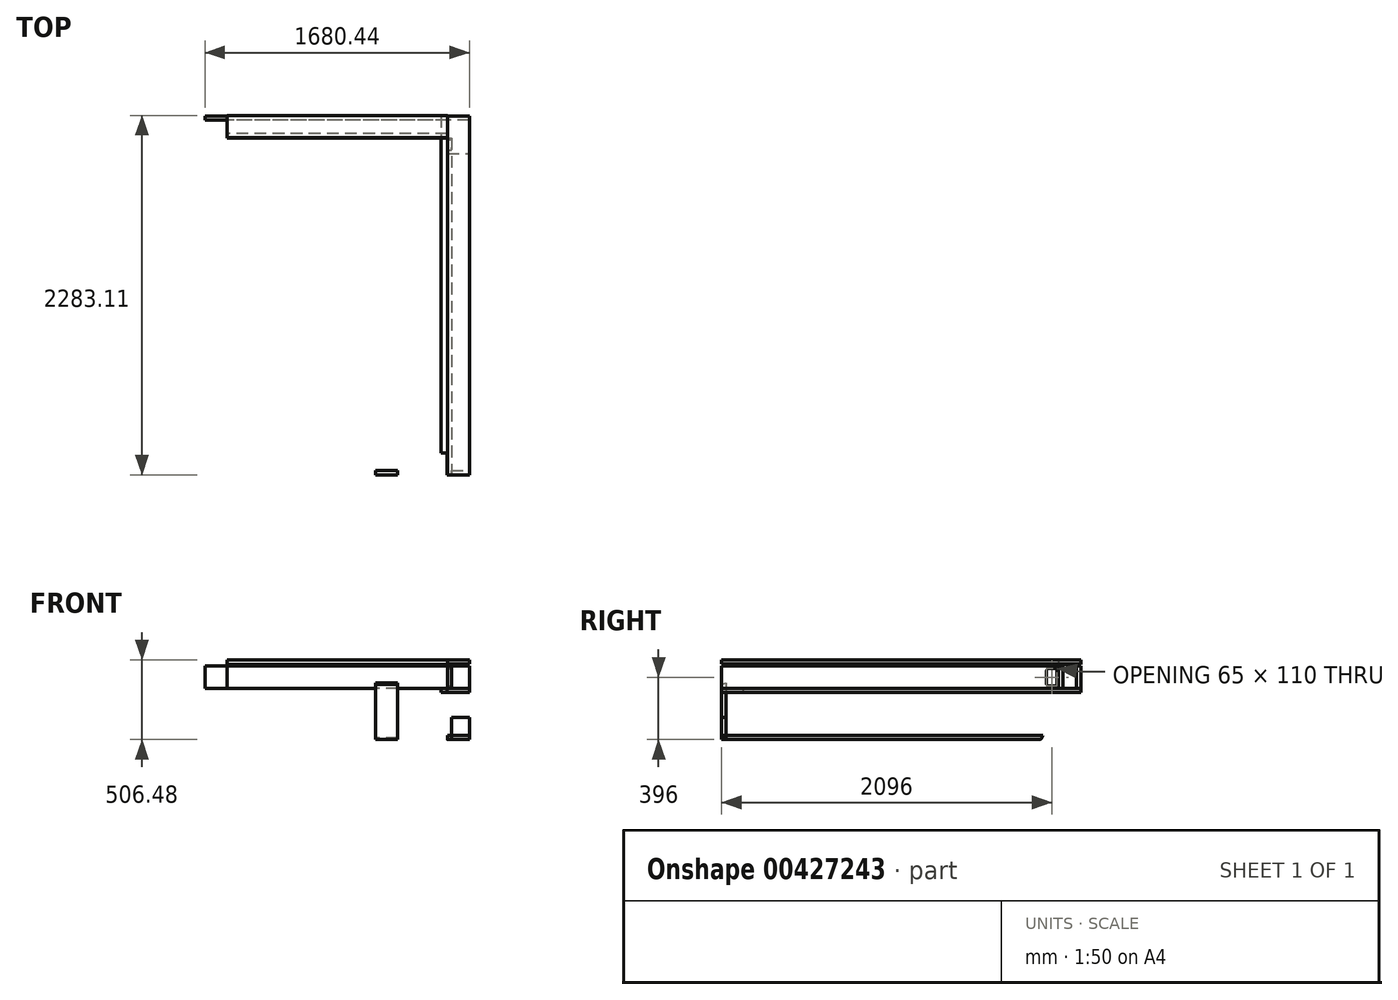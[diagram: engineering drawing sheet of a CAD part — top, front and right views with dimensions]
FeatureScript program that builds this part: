
annotation { "Feature Type Name" : "Feature", "Feature Type Description" : "" }
export const myFeature = defineFeature(function(context is Context, id is Id, definition is map)
    precondition{}
    {
        {
            var Q0;
            Q0=qCreatedBy(makeId("Front.planeOp"),FACE);
            var sketch = newSketch(context, id + "F0", { "sketchPlane" : qUnion([Q0])});
            skLineSegment(sketch, "E0.bottom", {"start": v(700, 0) * mm, "end": v(840, 0) * mm});
            skLineSegment(sketch, "E0.top", {"start": v(700, 26) * mm, "end": v(840, 26) * mm});
            skLineSegment(sketch, "E0.left", {"start": v(700, 0) * mm, "end": v(700, 26) * mm});
            skLineSegment(sketch, "E0.right", {"start": v(840, 0) * mm, "end": v(840, 26) * mm});
            skSolve(sketch);
        }
        {
            var Q0;
            Q0=makeQuery(id+"F0.imprint","IMPRINT",FACE,{"disambiguationData":[TD([[makeQuery(id+"F0.imprint","IMPRINT",EDGE,{"derivedFrom":sQuery(id+"F0.wireOp",EDGE,"E0.bottom")}),1.0]])]});
            extrude(context, id + "F1", {"entities" : qUnion([Q0]), "oppositeDirection" : true, "depth" : 2040 * mm});
        }
        {
            var Q0;
            Q0=makeQuery(id+"F1.opExtrude","CAP_EDGE",EDGE,{"disambiguationData":[OSD([sQuery(id+"F0.wireOp",EDGE,"E0.bottom")])],"isStart":true});
            var Q1;
            Q1=makeQuery(id+"F1.opExtrude","CAP_EDGE",EDGE,{"disambiguationData":[OSD([sQuery(id+"F0.wireOp",EDGE,"E0.bottom")])],"isStart":false});
            chamfer(context, id + "F2", {"entities" : qUnion([Q0, Q1]), "chamferType" : ChamferType.OFFSET_ANGLE, "width" : 26 * mm, "oppositeDirection" : false, "angle" : 20 * degree, "tangentPropagation" : true});
        }
        {
            var Q0;
            Q0=qCreatedBy(makeId("Front.planeOp"),FACE);
            var sketch = newSketch(context, id + "F3", { "sketchPlane" : qUnion([Q0])});
            skLineSegment(sketch, "E1.bottom", {"start": v(660, 300) * mm, "end": v(840, 300) * mm});
            skLineSegment(sketch, "E1.top", {"start": v(660, 326) * mm, "end": v(840, 326) * mm});
            skLineSegment(sketch, "E1.left", {"start": v(660, 300) * mm, "end": v(660, 326) * mm});
            skLineSegment(sketch, "E1.right", {"start": v(840, 300) * mm, "end": v(840, 326) * mm});
            skSolve(sketch);
        }
        {
            var Q0;
            Q0=makeQuery(id+"F3.imprint","IMPRINT",FACE,{"disambiguationData":[TD([[makeQuery(id+"F3.imprint","IMPRINT",EDGE,{"derivedFrom":sQuery(id+"F3.wireOp",EDGE,"E1.bottom")}),1.0]])]});
            extrude(context, id + "F4", {"entities" : qUnion([Q0]), "oppositeDirection" : true, "depth" : (2000 + (2 * 140)) * mm});
        }
        {
            var Q0;
            Q0=makeQuery(id+"F4.opExtrude","SWEPT_FACE",FACE,{"disambiguationData":[OSD([sQuery(id+"F3.wireOp",EDGE,"E1.top")])]});
            var sketch = newSketch(context, id + "F5", { "sketchPlane" : qUnion([Q0])});
            skLineSegment(sketch, "E2.bottom", {"start": v(659.64, 0) * mm, "end": v(699.64, 0) * mm});
            skLineSegment(sketch, "E2.top", {"start": v(659.64, 140) * mm, "end": v(699.64, 140) * mm});
            skLineSegment(sketch, "E2.left", {"start": v(659.64, 0) * mm, "end": v(659.64, 140) * mm});
            skLineSegment(sketch, "E2.right", {"start": v(699.64, 0) * mm, "end": v(699.64, 140) * mm});
            skSolve(sketch);
        }
        {
            var Q0;
            Q0 = qSketchRegion(id + "F5", true);
            extrude(context, id + "F6", {"entities" : qUnion([Q0]), "operationType" : NewBodyOperationType.REMOVE, "endBound" : BoundingType.UP_TO_NEXT, "oppositeDirection" : true, "depth" : 25 * mm});
        }
        {
            var Q0;
            Q0=qCreatedBy(makeId("Top.planeOp"),FACE);
            var sketch = newSketch(context, id + "F7", { "sketchPlane" : qUnion([Q0])});
            skLineSegment(sketch, "E3.bottom", {"start": v(726, 0) * mm, "end": v(840, 0) * mm});
            skLineSegment(sketch, "E3.top", {"start": v(726, 26) * mm, "end": v(840, 26) * mm});
            skLineSegment(sketch, "E3.left", {"start": v(726, 0) * mm, "end": v(726, 26) * mm});
            skLineSegment(sketch, "E3.right", {"start": v(840, 0) * mm, "end": v(840, 26) * mm});
            skSolve(sketch);
        }
        {
            var Q0;
            Q0=makeQuery(id+"F7.imprint","IMPRINT",FACE,{"disambiguationData":[TD([[makeQuery(id+"F7.imprint","IMPRINT",EDGE,{"derivedFrom":sQuery(id+"F7.wireOp",EDGE,"E3.bottom")}),1.0]])]});
            extrude(context, id + "F8", {"entities" : qUnion([Q0]), "depth" : 140 * mm});
        }
        {
            var Q0;
            Q0=qCreatedBy(makeId("Front.planeOp"),FACE);
            var sketch = newSketch(context, id + "F9", { "sketchPlane" : qUnion([Q0])});
            skLineSegment(sketch, "E4.top", {"start": v(700, 466) * mm, "end": v(726, 466) * mm});
            skLineSegment(sketch, "E4.left", {"start": v(700, 326) * mm, "end": v(700, 466) * mm});
            skLineSegment(sketch, "E4.right", {"start": v(726, 326) * mm, "end": v(726, 466) * mm});
            skLineSegment(sketch, "E5", {"start": v(700, 326) * mm, "end": v(726, 326) * mm});
            skSolve(sketch);
        }
        {
            var Q0;
            Q0 = qSketchRegion(id + "F9", true);
            extrude(context, id + "F10", {"entities" : qUnion([Q0]), "oppositeDirection" : true, "depth" : (2000 + 140) * mm});
        }
        {
            var Q0;
            Q0=makeQuery(id+"F10.opExtrude","SWEPT_FACE",FACE,{"disambiguationData":[OSD([sQuery(id+"F9.wireOp",EDGE,"E4.right")])]});
            var sketch = newSketch(context, id + "F11", { "sketchPlane" : qUnion([Q0])});
            skLineSegment(sketch, "E6", {"start": v(2140, 396) * mm, "end": v(2052, 396) * mm, "construction": true});
            skLineSegment(sketch, "E7.bottom", {"start": v(2113.5, 451) * mm, "end": v(2078.5, 451) * mm});
            skLineSegment(sketch, "E7.top", {"start": v(2113.5, 341) * mm, "end": v(2078.5, 341) * mm});
            skLineSegment(sketch, "E7.left", {"start": v(2128.5, 436) * mm, "end": v(2128.5, 356) * mm});
            skLineSegment(sketch, "E7.right", {"start": v(2063.5, 436) * mm, "end": v(2063.5, 356) * mm});
            skPoint(sketch, "E7.middle", {"position": v(2096, 396) * mm});
            skPoint(sketch, "E8.visualSharp", {"position": v(2063.5, 451) * mm});
            skArc(sketch, "E8.filletArc", {"start": v(2078.5, 451) * mm, "mid": v(2067.9, 446.6) * mm, "end": v(2063.5, 436) * mm});
            skPoint(sketch, "E9.visualSharp", {"position": v(2128.5, 451) * mm});
            skArc(sketch, "E9.filletArc", {"start": v(2128.5, 436) * mm, "mid": v(2124.1, 446.6) * mm, "end": v(2113.5, 451) * mm});
            skPoint(sketch, "E10.visualSharp", {"position": v(2128.5, 341) * mm});
            skArc(sketch, "E10.filletArc", {"start": v(2113.5, 341) * mm, "mid": v(2124.1, 345.4) * mm, "end": v(2128.5, 356) * mm});
            skPoint(sketch, "E11.visualSharp", {"position": v(2063.5, 341) * mm});
            skArc(sketch, "E11.filletArc", {"start": v(2063.5, 356) * mm, "mid": v(2067.9, 345.4) * mm, "end": v(2078.5, 341) * mm});
            skSolve(sketch);
        }
        {
            var Q0;
            Q0=qCreatedBy(makeId("Right.planeOp"),FACE);
            var sketch = newSketch(context, id + "F12", { "sketchPlane" : qUnion([Q0])});
            skLineSegment(sketch, "E12.bottom", {"start": v(2254, 326) * mm, "end": v(2280, 326) * mm});
            skLineSegment(sketch, "E12.top", {"start": v(2254, 466) * mm, "end": v(2280, 466) * mm});
            skLineSegment(sketch, "E12.left", {"start": v(2254, 326) * mm, "end": v(2254, 466) * mm});
            skLineSegment(sketch, "E12.right", {"start": v(2280, 326) * mm, "end": v(2280, 466) * mm});
            skSolve(sketch);
        }
        {
            var Q0;
            Q0 = qSketchRegion(id + "F12", true);
            extrude(context, id + "F13", {"entities" : qUnion([Q0]), "endBound" : BoundingType.SYMMETRIC, "depth" : (1400 + (2 * 140)) * mm});
        }
        {
            var Q0;
            Q0=qCreatedBy(makeId("Right.planeOp"),FACE);
            var sketch = newSketch(context, id + "F14", { "sketchPlane" : qUnion([Q0])});
            skLineSegment(sketch, "E13.bottom", {"start": v(2140, 326) * mm, "end": v(2166, 326) * mm});
            skLineSegment(sketch, "E13.top", {"start": v(2140, 466) * mm, "end": v(2166, 466) * mm});
            skLineSegment(sketch, "E13.left", {"start": v(2140, 326) * mm, "end": v(2140, 466) * mm});
            skLineSegment(sketch, "E13.right", {"start": v(2166, 326) * mm, "end": v(2166, 466) * mm});
            skSolve(sketch);
        }
        {
            var Q0;
            Q0 = qSketchRegion(id + "F14", true);
            extrude(context, id + "F15", {"entities" : qUnion([Q0]), "endBound" : BoundingType.SYMMETRIC, "depth" : 1400 * mm});
        }
        {
            var Q0;
            Q0=qCreatedBy(makeId("Top.planeOp"),FACE);
            var sketch = newSketch(context, id + "F16", { "sketchPlane" : qUnion([Q0])});
            skLineSegment(sketch, "E14.bottom", {"start": v(244.36, 0) * mm, "end": v(384.36, 0) * mm});
            skLineSegment(sketch, "E14.top", {"start": v(244.36, 26) * mm, "end": v(384.36, 26) * mm});
            skLineSegment(sketch, "E14.left", {"start": v(244.36, 0) * mm, "end": v(244.36, 26) * mm});
            skLineSegment(sketch, "E14.right", {"start": v(384.36, 0) * mm, "end": v(384.36, 26) * mm});
            skSolve(sketch);
        }
        {
            var Q0;
            Q0 = qSketchRegion(id + "F16", true);
            extrude(context, id + "F17", {"entities" : qUnion([Q0]), "depth" : 360 * mm});
        }
        {
            var Q0;
            Q0=makeQuery(id+"F17.opExtrude","CAP_EDGE",EDGE,{"disambiguationData":[OSD([sQuery(id+"F16.wireOp",EDGE,"E14.bottom")])],"isStart":false});
            var Q1;
            Q1=makeQuery(id+"F17.opExtrude","CAP_EDGE",EDGE,{"disambiguationData":[OSD([sQuery(id+"F16.wireOp",EDGE,"E14.top")])],"isStart":true});
            chamfer(context, id + "F18", {"entities" : qUnion([Q0, Q1]), "chamferType" : ChamferType.OFFSET_ANGLE, "width" : 26 * mm, "oppositeDirection" : false, "angle" : 20 * degree, "tangentPropagation" : true});
        }
        {
            var Q0;
            Q0=qCreatedBy(makeId("Right.planeOp"),FACE);
            var sketch = newSketch(context, id + "F19", { "sketchPlane" : qUnion([Q0])});
            skLineSegment(sketch, "E15.bottom", {"start": v(2283.11, 478.5) * mm, "end": v(2143.11, 478.5) * mm});
            skLineSegment(sketch, "E15.top", {"start": v(2283.11, 504.5) * mm, "end": v(2143.11, 504.5) * mm});
            skLineSegment(sketch, "E15.left", {"start": v(2283.11, 478.5) * mm, "end": v(2283.11, 504.5) * mm});
            skLineSegment(sketch, "E15.right", {"start": v(2143.11, 478.5) * mm, "end": v(2143.11, 504.5) * mm});
            skSolve(sketch);
        }
        {
            var Q0;
            Q0 = qSketchRegion(id + "F19", true);
            extrude(context, id + "F20", {"entities" : qUnion([Q0]), "endBound" : BoundingType.SYMMETRIC, "depth" : 1400 * mm});
        }
        {
            var Q0;
            Q0=qCreatedBy(makeId("Front.planeOp"),FACE);
            var sketch = newSketch(context, id + "F21", { "sketchPlane" : qUnion([Q0])});
            skLineSegment(sketch, "E16.bottom", {"start": v(700.44, 480.48) * mm, "end": v(840.44, 480.48) * mm});
            skLineSegment(sketch, "E16.top", {"start": v(700.44, 506.48) * mm, "end": v(840.44, 506.48) * mm});
            skLineSegment(sketch, "E16.left", {"start": v(700.44, 480.48) * mm, "end": v(700.44, 506.48) * mm});
            skLineSegment(sketch, "E16.right", {"start": v(840.44, 480.48) * mm, "end": v(840.44, 506.48) * mm});
            skSolve(sketch);
        }
        {
            var Q0;
            Q0=makeQuery(id+"F21.imprint","IMPRINT",FACE,{"disambiguationData":[TD([[makeQuery(id+"F21.imprint","IMPRINT",EDGE,{"derivedFrom":sQuery(id+"F21.wireOp",EDGE,"E16.bottom")}),1.0]])]});
            extrude(context, id + "F22", {"entities" : qUnion([Q0]), "oppositeDirection" : true, "depth" : ((2000 + (2 * 140))) * mm});
        }
        {
            var Q0;
            Q0=makeQuery(id+"F11.imprint","IMPRINT",FACE,{"disambiguationData":[TD([[makeQuery(id+"F11.imprint","IMPRINT",EDGE,{"derivedFrom":sQuery(id+"F11.wireOp",EDGE,"E7.bottom")}),1.0]])]});
            extrude(context, id + "F23", {"entities" : qUnion([Q0]), "operationType" : NewBodyOperationType.REMOVE, "endBound" : BoundingType.THROUGH_ALL, "oppositeDirection" : true, "depth" : 25 * mm});
        }
        {
            var Q0;
            {var subQ0=sQuery(id+"F0.wireOp",EDGE,"E0.bottom");Q0=makeQuery(id+"F2.opChamfer","BLEND_EDGE",EDGE,{"blendedFrom":[makeQuery(id+"F1.opExtrude","CAP_EDGE",EDGE,{"disambiguationData":[OSD([subQ0])],"isStart":true}),makeQuery(id+"F1.opExtrude","SWEPT_FACE",FACE,{"disambiguationData":[OSD([subQ0])]})],"blendedInto":[makeQuery(id+"F1.opExtrude","SWEPT_FACE",FACE,{"disambiguationData":[OSD([subQ0])]})]});}
            var Q1;
            {var subQ0=sQuery(id+"F0.wireOp",EDGE,"E0.bottom");Q1=makeQuery(id+"F2.opChamfer","BLEND_EDGE",EDGE,{"blendedFrom":[makeQuery(id+"F1.opExtrude","CAP_EDGE",EDGE,{"disambiguationData":[OSD([subQ0])],"isStart":false}),makeQuery(id+"F1.opExtrude","SWEPT_FACE",FACE,{"disambiguationData":[OSD([subQ0])]})],"blendedInto":[makeQuery(id+"F1.opExtrude","SWEPT_FACE",FACE,{"disambiguationData":[OSD([subQ0])]})]});}
            fillet(context, id + "F24", {"entities" : qUnion([Q0, Q1]), "radius" : 20 * mm, "tangentPropagation" : true, "allowEdgeOverflow" : false});
        }
    });
